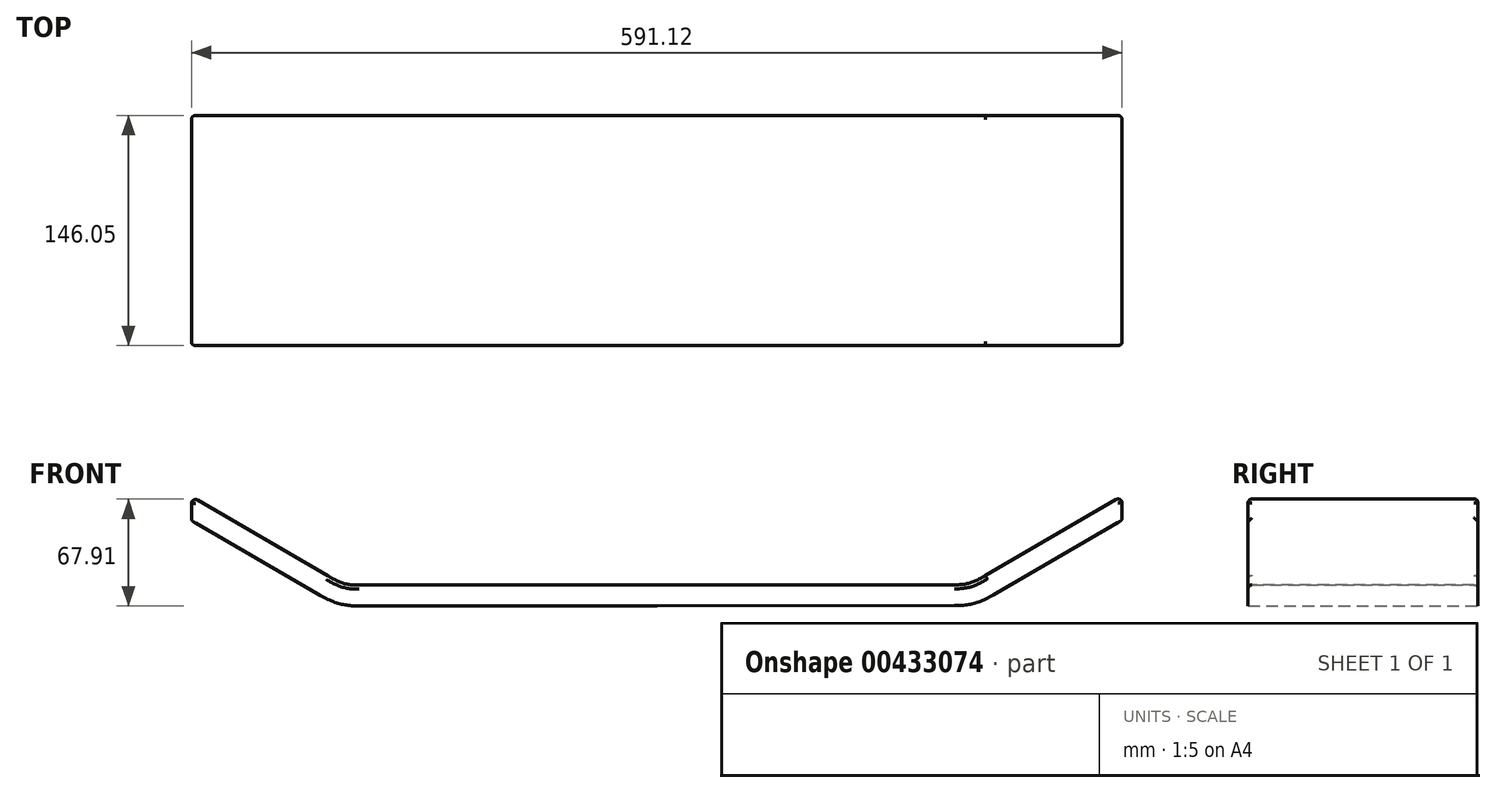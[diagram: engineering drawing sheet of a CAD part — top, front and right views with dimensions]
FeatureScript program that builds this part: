
annotation { "Feature Type Name" : "Feature", "Feature Type Description" : "" }
export const myFeature = defineFeature(function(context is Context, id is Id, definition is map)
    precondition{}
    {
        {
            var Q0;
            Q0=qCreatedBy(makeId("Front.planeOp"),FACE);
            var sketch = newSketch(context, id + "F0", { "sketchPlane" : qUnion([Q0])});
            skLineSegment(sketch, "E0", {"start": v(1.6, 54.16) * mm, "end": v(81.9, 7.54) * mm});
            skFitSpline(sketch, "E1", {"points": [v(81.9, 7.54) * mm, v(108.17, 0) * mm], "startDerivative": vector(31.2, -18.1) * mm, "endDerivative": vector(28.65, 0) * mm});
            skLineSegment(sketch, "E2", {"start": v(108.17, 0) * mm, "end": v(297.19, 0) * mm});
            skLineSegment(sketch, "E3", {"start": v(1.6, 65.9) * mm, "end": v(1.6, 54.16) * mm});
            skLineSegment(sketch, "E4", {"start": v(297.19, 0) * mm, "end": v(163.84, 0) * mm});
            skLineSegment(sketch, "E5.bottom", {"start": v(163.84, 0) * mm, "end": v(138.44, 0) * mm});
            skLineSegment(sketch, "E6", {"start": v(297.18, 10.16) * mm, "end": v(297.19, 0) * mm});
            skLineSegment(sketch, "E7.0", {"start": v(8.22, 65.58) * mm, "end": v(3.12, 68.54) * mm});
            skLineSegment(sketch, "E7.1", {"start": v(8.22, 65.58) * mm, "end": v(88.53, 18.96) * mm});
            skFitSpline(sketch, "E7.2", {"points": [v(88.53, 18.96) * mm, v(89.68, 18.3) * mm, v(91.81, 17.12) * mm, v(94.53, 15.8) * mm, v(96.85, 14.86) * mm, v(98.9, 14.2) * mm, v(100.86, 13.74) * mm, v(102.92, 13.43) * mm, v(105.29, 13.25) * mm, v(107.15, 13.2) * mm, v(108.17, 13.2) * mm]});
            skLineSegment(sketch, "E7.3", {"start": v(108.17, 13.2) * mm, "end": v(297.18, 13.2) * mm});
            skLineSegment(sketch, "E8", {"start": v(297.18, 13.2) * mm, "end": v(297.18, 10.16) * mm});
            skLineSegment(sketch, "E9", {"start": v(3.12, 68.54) * mm, "end": v(1.6, 69.43) * mm});
            skLineSegment(sketch, "E10", {"start": v(1.6, 65.9) * mm, "end": v(1.6, 69.43) * mm});
            skSolve(sketch);
        }
        {
            var Q0;
            Q0=makeQuery(id+"F0.imprint","IMPRINT",FACE,{"disambiguationData":[TD([[makeQuery(id+"F0.imprint","IMPRINT",EDGE,{"derivedFrom":sQuery(id+"F0.wireOp",EDGE,"E5.bottom")}),1.0]])]});
            var Q1;
            Q1=makeQuery(id+"F0.imprint","IMPRINT",FACE,{"disambiguationData":[TD([[makeQuery(id+"F0.imprint","IMPRINT",EDGE,{"derivedFrom":sQuery(id+"F0.wireOp",EDGE,"E0")}),1.0]])]});
            extrude(context, id + "F1", {"entities" : qUnion([Q0, Q1]), "depth" : 146.05 * mm});
        }
        {
            var Q0;
            Q0=makeQuery(id+"F1.opExtrude","CAP_EDGE",EDGE,{"disambiguationData":[OSD([sQuery(id+"F0.wireOp",EDGE,"ea2c2fc9-0261-4e25-8d83-237bf5a555dd.0")])],"isStart":true});
            var Q1;
            Q1=makeQuery(id+"F1.opExtrude","CAP_EDGE",EDGE,{"disambiguationData":[OSD([sQuery(id+"F0.wireOp",EDGE,"ea2c2fc9-0261-4e25-8d83-237bf5a555dd.1")])],"isStart":true});
            var Q2;
            Q2=makeQuery(id+"F1.opExtrude","CAP_EDGE",EDGE,{"disambiguationData":[OSD([sQuery(id+"F0.wireOp",EDGE,"ea2c2fc9-0261-4e25-8d83-237bf5a555dd.2"),sQuery(id+"F0.wireOp",EDGE,"udcYPTew-gpvt-nIya-2NXr-ynJiULjF3jXy")])],"isStart":true});
            var Q3;
            Q3=makeQuery(id+"F1.opExtrude","SWEPT_EDGE",EDGE,{"disambiguationData":[OSD([sQuery(id+"F0.wireOp",EDGE,"udcYPTew-gpvt-nIya-2NXr-ynJiULjF3jXy"),sQuery(id+"F0.wireOp",EDGE,"E3")])]});
            var Q4;
            Q4=makeQuery(id+"F1.opExtrude","CAP_EDGE",EDGE,{"disambiguationData":[OSD([sQuery(id+"F0.wireOp",EDGE,"ea2c2fc9-0261-4e25-8d83-237bf5a555dd.2"),sQuery(id+"F0.wireOp",EDGE,"udcYPTew-gpvt-nIya-2NXr-ynJiULjF3jXy")])],"isStart":false});
            var Q5;
            Q5=makeQuery(id+"F1.opExtrude","CAP_EDGE",EDGE,{"disambiguationData":[OSD([sQuery(id+"F0.wireOp",EDGE,"ea2c2fc9-0261-4e25-8d83-237bf5a555dd.1")])],"isStart":false});
            var Q6;
            Q6=makeQuery(id+"F1.opExtrude","CAP_EDGE",EDGE,{"disambiguationData":[OSD([sQuery(id+"F0.wireOp",EDGE,"ea2c2fc9-0261-4e25-8d83-237bf5a555dd.0")])],"isStart":false});
            var Q7;
            Q7=makeQuery(id+"F1.opExtrude","CAP_EDGE",EDGE,{"disambiguationData":[OSD([sQuery(id+"F0.wireOp",EDGE,"E3")])],"isStart":false});
            var Q8;
            Q8=makeQuery(id+"F1.opExtrude","CAP_EDGE",EDGE,{"disambiguationData":[OSD([sQuery(id+"F0.wireOp",EDGE,"E3")])],"isStart":true});
            fillet(context, id + "F2", {"entities" : qUnion([Q0, Q1, Q2, Q3, Q4, Q5, Q6, Q7, Q8]), "radius" : 2.54 * mm, "tangentPropagation" : true, "allowEdgeOverflow" : false});
        }
        {
            var Q0;
            Q0=makeQuery(id+"F1.opExtrude","SWEPT_BODY",BODY,{"disambiguationData":[OSD([sQuery(id+"F0.wireOp",EDGE,"E0"),sQuery(id+"F0.wireOp",EDGE,"E1"),sQuery(id+"F0.wireOp",EDGE,"E2"),sQuery(id+"F0.wireOp",EDGE,"ea2c2fc9-0261-4e25-8d83-237bf5a555dd.0"),sQuery(id+"F0.wireOp",EDGE,"ea2c2fc9-0261-4e25-8d83-237bf5a555dd.1"),sQuery(id+"F0.wireOp",EDGE,"ea2c2fc9-0261-4e25-8d83-237bf5a555dd.2"),sQuery(id+"F0.wireOp",EDGE,"udcYPTew-gpvt-nIya-2NXr-ynJiULjF3jXy"),sQuery(id+"F0.wireOp",EDGE,"E3"),sQuery(id+"F0.wireOp",EDGE,"E4"),sQuery(id+"F0.wireOp",EDGE,"E5.bottom"),sQuery(id+"F0.wireOp",EDGE,"E6")])]});
            var Q1;
            Q1=makeQuery(id+"F1.opExtrude","SWEPT_FACE",FACE,{"disambiguationData":[OSD([sQuery(id+"F0.wireOp",EDGE,"E6")])]});
            mirror(context, id + "F3", {"operationType" : NewBodyOperationType.ADD, "entities" : qUnion([Q0]), "mirrorPlane" : qUnion([Q1])});
        }
        {
            var Q0;
            Q0=makeQuery(id+"F1.opExtrude","SWEPT_BODY",BODY,{"disambiguationData":[OSD([sQuery(id+"F0.wireOp",EDGE,"E0"),sQuery(id+"F0.wireOp",EDGE,"E1"),sQuery(id+"F0.wireOp",EDGE,"E2"),sQuery(id+"F0.wireOp",EDGE,"ea2c2fc9-0261-4e25-8d83-237bf5a555dd.0"),sQuery(id+"F0.wireOp",EDGE,"ea2c2fc9-0261-4e25-8d83-237bf5a555dd.1"),sQuery(id+"F0.wireOp",EDGE,"ea2c2fc9-0261-4e25-8d83-237bf5a555dd.2"),sQuery(id+"F0.wireOp",EDGE,"udcYPTew-gpvt-nIya-2NXr-ynJiULjF3jXy"),sQuery(id+"F0.wireOp",EDGE,"E3"),sQuery(id+"F0.wireOp",EDGE,"E4"),sQuery(id+"F0.wireOp",EDGE,"E5.bottom"),sQuery(id+"F0.wireOp",EDGE,"E6")])]});
            transform(context, id + "F4", {"entities" : qUnion([Q0]), "transformType" : TransformType.TRANSLATION_3D, "dx" : 0 * mm, "dy" : 190.5 * mm, "dz" : 0 * mm, "makeCopy" : true});
        }
        {
            var Q0;
            Q0=makeQuery(id+"F4.opPattern","COPY",BODY,{"derivedFrom":makeQuery(id+"F1.opExtrude","SWEPT_BODY",BODY,{"disambiguationData":[OSD([sQuery(id+"F0.wireOp",EDGE,"E0"),sQuery(id+"F0.wireOp",EDGE,"E1"),sQuery(id+"F0.wireOp",EDGE,"E2"),sQuery(id+"F0.wireOp",EDGE,"ea2c2fc9-0261-4e25-8d83-237bf5a555dd.0"),sQuery(id+"F0.wireOp",EDGE,"ea2c2fc9-0261-4e25-8d83-237bf5a555dd.1"),sQuery(id+"F0.wireOp",EDGE,"ea2c2fc9-0261-4e25-8d83-237bf5a555dd.2"),sQuery(id+"F0.wireOp",EDGE,"udcYPTew-gpvt-nIya-2NXr-ynJiULjF3jXy"),sQuery(id+"F0.wireOp",EDGE,"E3"),sQuery(id+"F0.wireOp",EDGE,"E4"),sQuery(id+"F0.wireOp",EDGE,"E5.bottom"),sQuery(id+"F0.wireOp",EDGE,"E6")])]}),"instanceName":"1"});
            transform(context, id + "F5", {"entities" : qUnion([Q0]), "transformType" : TransformType.TRANSLATION_3D, "dx" : 0 * mm, "dy" : 190.5 * mm, "dz" : 0 * mm, "makeCopy" : true});
        }
        {
            var Q0;
            Q0=makeQuery(id+"F5.opPattern","COPY",BODY,{"derivedFrom":makeQuery(id+"F4.opPattern","COPY",BODY,{"derivedFrom":makeQuery(id+"F1.opExtrude","SWEPT_BODY",BODY,{"disambiguationData":[OSD([sQuery(id+"F0.wireOp",EDGE,"E0"),sQuery(id+"F0.wireOp",EDGE,"E1"),sQuery(id+"F0.wireOp",EDGE,"E2"),sQuery(id+"F0.wireOp",EDGE,"ea2c2fc9-0261-4e25-8d83-237bf5a555dd.0"),sQuery(id+"F0.wireOp",EDGE,"ea2c2fc9-0261-4e25-8d83-237bf5a555dd.1"),sQuery(id+"F0.wireOp",EDGE,"ea2c2fc9-0261-4e25-8d83-237bf5a555dd.2"),sQuery(id+"F0.wireOp",EDGE,"udcYPTew-gpvt-nIya-2NXr-ynJiULjF3jXy"),sQuery(id+"F0.wireOp",EDGE,"E3"),sQuery(id+"F0.wireOp",EDGE,"E4"),sQuery(id+"F0.wireOp",EDGE,"E5.bottom"),sQuery(id+"F0.wireOp",EDGE,"E6")])]}),"instanceName":"1"}),"instanceName":"1"});
            transform(context, id + "F6", {"entities" : qUnion([Q0]), "transformType" : TransformType.TRANSLATION_3D, "dx" : 0 * mm, "dy" : 190.5 * mm, "dz" : 0 * mm, "makeCopy" : true});
        }
        {
            var Q0;
            Q0=makeQuery(id+"F6.opPattern","COPY",BODY,{"derivedFrom":makeQuery(id+"F5.opPattern","COPY",BODY,{"derivedFrom":makeQuery(id+"F4.opPattern","COPY",BODY,{"derivedFrom":makeQuery(id+"F1.opExtrude","SWEPT_BODY",BODY,{"disambiguationData":[OSD([sQuery(id+"F0.wireOp",EDGE,"E0"),sQuery(id+"F0.wireOp",EDGE,"E1"),sQuery(id+"F0.wireOp",EDGE,"E2"),sQuery(id+"F0.wireOp",EDGE,"ea2c2fc9-0261-4e25-8d83-237bf5a555dd.0"),sQuery(id+"F0.wireOp",EDGE,"ea2c2fc9-0261-4e25-8d83-237bf5a555dd.1"),sQuery(id+"F0.wireOp",EDGE,"ea2c2fc9-0261-4e25-8d83-237bf5a555dd.2"),sQuery(id+"F0.wireOp",EDGE,"udcYPTew-gpvt-nIya-2NXr-ynJiULjF3jXy"),sQuery(id+"F0.wireOp",EDGE,"E3"),sQuery(id+"F0.wireOp",EDGE,"E4"),sQuery(id+"F0.wireOp",EDGE,"E5.bottom"),sQuery(id+"F0.wireOp",EDGE,"E6")])]}),"instanceName":"1"}),"instanceName":"1"}),"instanceName":"1"});
            var Q1;
            Q1=makeQuery(id+"F5.opPattern","COPY",BODY,{"derivedFrom":makeQuery(id+"F4.opPattern","COPY",BODY,{"derivedFrom":makeQuery(id+"F1.opExtrude","SWEPT_BODY",BODY,{"disambiguationData":[OSD([sQuery(id+"F0.wireOp",EDGE,"E0"),sQuery(id+"F0.wireOp",EDGE,"E1"),sQuery(id+"F0.wireOp",EDGE,"E2"),sQuery(id+"F0.wireOp",EDGE,"ea2c2fc9-0261-4e25-8d83-237bf5a555dd.0"),sQuery(id+"F0.wireOp",EDGE,"ea2c2fc9-0261-4e25-8d83-237bf5a555dd.1"),sQuery(id+"F0.wireOp",EDGE,"ea2c2fc9-0261-4e25-8d83-237bf5a555dd.2"),sQuery(id+"F0.wireOp",EDGE,"udcYPTew-gpvt-nIya-2NXr-ynJiULjF3jXy"),sQuery(id+"F0.wireOp",EDGE,"E3"),sQuery(id+"F0.wireOp",EDGE,"E4"),sQuery(id+"F0.wireOp",EDGE,"E5.bottom"),sQuery(id+"F0.wireOp",EDGE,"E6")])]}),"instanceName":"1"}),"instanceName":"1"});
            var Q2;
            Q2=makeQuery(id+"F4.opPattern","COPY",BODY,{"derivedFrom":makeQuery(id+"F1.opExtrude","SWEPT_BODY",BODY,{"disambiguationData":[OSD([sQuery(id+"F0.wireOp",EDGE,"E0"),sQuery(id+"F0.wireOp",EDGE,"E1"),sQuery(id+"F0.wireOp",EDGE,"E2"),sQuery(id+"F0.wireOp",EDGE,"ea2c2fc9-0261-4e25-8d83-237bf5a555dd.0"),sQuery(id+"F0.wireOp",EDGE,"ea2c2fc9-0261-4e25-8d83-237bf5a555dd.1"),sQuery(id+"F0.wireOp",EDGE,"ea2c2fc9-0261-4e25-8d83-237bf5a555dd.2"),sQuery(id+"F0.wireOp",EDGE,"udcYPTew-gpvt-nIya-2NXr-ynJiULjF3jXy"),sQuery(id+"F0.wireOp",EDGE,"E3"),sQuery(id+"F0.wireOp",EDGE,"E4"),sQuery(id+"F0.wireOp",EDGE,"E5.bottom"),sQuery(id+"F0.wireOp",EDGE,"E6")])]}),"instanceName":"1"});
            deleteBodies(context, id + "F7", {"entities" : qUnion([Q0, Q1, Q2])});
        }
        {
            var Q0;
            Q0=makeQuery(id+"F3.opPattern","COPY",EDGE,{"derivedFrom":makeQuery(id+"F1.opExtrude","CAP_EDGE",EDGE,{"disambiguationData":[OSD([sQuery(id+"F0.wireOp",EDGE,"E7.0"),sQuery(id+"F0.wireOp",EDGE,"E7.1"),sQuery(id+"F0.wireOp",EDGE,"E9")])],"isStart":true}),"instanceName":"1"});
            var Q1;
            Q1=makeQuery(id+"F3.opPattern","COPY",EDGE,{"derivedFrom":makeQuery(id+"F1.opExtrude","SWEPT_EDGE",EDGE,{"disambiguationData":[OSD([sQuery(id+"F0.wireOp",EDGE,"E9"),sQuery(id+"F0.wireOp",EDGE,"E10")])]}),"instanceName":"1"});
            var Q2;
            Q2=makeQuery(id+"F3.opPattern","COPY",EDGE,{"derivedFrom":makeQuery(id+"F1.opExtrude","CAP_EDGE",EDGE,{"disambiguationData":[OSD([sQuery(id+"F0.wireOp",EDGE,"E7.0"),sQuery(id+"F0.wireOp",EDGE,"E7.1"),sQuery(id+"F0.wireOp",EDGE,"E9")])],"isStart":false}),"instanceName":"1"});
            var Q3;
            Q3=makeQuery(id+"F3.opPattern","COPY",EDGE,{"derivedFrom":makeQuery(id+"F1.opExtrude","CAP_EDGE",EDGE,{"disambiguationData":[OSD([sQuery(id+"F0.wireOp",EDGE,"E7.2")])],"isStart":false}),"instanceName":"1"});
            var Q4;
            Q4=makeQuery(id+"F3.opPattern","COPY",EDGE,{"derivedFrom":makeQuery(id+"F1.opExtrude","CAP_EDGE",EDGE,{"disambiguationData":[OSD([sQuery(id+"F0.wireOp",EDGE,"E7.2")])],"isStart":true}),"instanceName":"1"});
            var Q5;
            Q5=makeQuery(id+"F3.opPattern","COPY",EDGE,{"derivedFrom":makeQuery(id+"F1.opExtrude","CAP_EDGE",EDGE,{"disambiguationData":[OSD([sQuery(id+"F0.wireOp",EDGE,"E7.3")])],"isStart":false}),"instanceName":"1"});
            var Q6;
            Q6=makeQuery(id+"F3.opPattern","COPY",EDGE,{"derivedFrom":makeQuery(id+"F1.opExtrude","CAP_EDGE",EDGE,{"disambiguationData":[OSD([sQuery(id+"F0.wireOp",EDGE,"E7.3")])],"isStart":true}),"instanceName":"1"});
            var Q7;
            Q7=makeQuery(id+"F1.opExtrude","CAP_EDGE",EDGE,{"disambiguationData":[OSD([sQuery(id+"F0.wireOp",EDGE,"E7.3")])],"isStart":true});
            var Q8;
            Q8=makeQuery(id+"F1.opExtrude","CAP_EDGE",EDGE,{"disambiguationData":[OSD([sQuery(id+"F0.wireOp",EDGE,"E7.3")])],"isStart":false});
            var Q9;
            Q9=makeQuery(id+"F1.opExtrude","CAP_EDGE",EDGE,{"disambiguationData":[OSD([sQuery(id+"F0.wireOp",EDGE,"E7.2")])],"isStart":false});
            var Q10;
            Q10=makeQuery(id+"F1.opExtrude","CAP_EDGE",EDGE,{"disambiguationData":[OSD([sQuery(id+"F0.wireOp",EDGE,"E7.2")])],"isStart":true});
            var Q11;
            Q11=makeQuery(id+"F1.opExtrude","CAP_EDGE",EDGE,{"disambiguationData":[OSD([sQuery(id+"F0.wireOp",EDGE,"E7.0"),sQuery(id+"F0.wireOp",EDGE,"E7.1"),sQuery(id+"F0.wireOp",EDGE,"E9")])],"isStart":true});
            var Q12;
            Q12=makeQuery(id+"F1.opExtrude","CAP_EDGE",EDGE,{"disambiguationData":[OSD([sQuery(id+"F0.wireOp",EDGE,"E7.0"),sQuery(id+"F0.wireOp",EDGE,"E7.1"),sQuery(id+"F0.wireOp",EDGE,"E9")])],"isStart":false});
            var Q13;
            Q13=makeQuery(id+"F1.opExtrude","SWEPT_EDGE",EDGE,{"disambiguationData":[OSD([sQuery(id+"F0.wireOp",EDGE,"E9"),sQuery(id+"F0.wireOp",EDGE,"E10")])]});
            fillet(context, id + "F8", {"entities" : qUnion([Q0, Q1, Q2, Q3, Q4, Q5, Q6, Q7, Q8, Q9, Q10, Q11, Q12, Q13]), "radius" : 2.54 * mm, "tangentPropagation" : true, "allowEdgeOverflow" : false});
        }
    });
